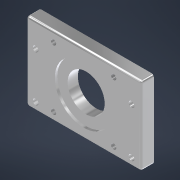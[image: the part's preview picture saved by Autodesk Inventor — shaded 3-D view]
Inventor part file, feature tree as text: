
AUTODESK INVENTOR PART (.ipt)
format: ipt  version: 2022 (Build 260153000, 153)  size: 172,032 bytes
history: native  units: mm
features: other x8, reference x6, sketch x3, extrude x2, hole x2, fillet x1, projected_geometry x1
ambient origin geometry x8: Origin, YZ Plane, XZ Plane, XY Plane, X Axis, Y Axis, Z Axis, Center Point
bodies: Solid1 (feature_tree)
feature tree (23):
  extrude  "Extrusion1"  Depth=8.0mm
  extrude  "Extrusion2"  Depth=2.0mm
  hole  "Hole2"  [1 undecoded]
  hole  "Hole3"  [1 undecoded]
  fillet  "Fillet1"  Radius=36.0mm
  sketch  "Sketch1"  dims[d2=8.0mm d3=0.0mm d6=31.0mm]
  reference  "Reference1"
  sketch  "Sketch6"  dims[d7=30.0mm]
  projected_geometry  "Projected Loop1"
  sketch  "Sketch7"  dims[d18=4.134mm d19=7.0mm d20=8.0mm d21=4.6mm d22=90.0deg d23=8.2mm d24=20.594885mm d25=45.0mm d26=2.0mm d27=0.0mm d28=75.0mm d29=36.0mm d30=6.0mm d31=4.5mm d32=6.0mm d33=8.0mm d34=4.6mm d35=90.0deg d36=8.0mm d37=20.594885mm d38=2.0mm d39=2.0mm d40=1.0mm d41=1.0mm d42=1.0mm d43=0.15mm d44=0.25mm d45=0.375mm d46=14.3117mm d47=0.75mm d48=20.594885mm d49=0.0625mm d50=0.75mm d51=0.375mm]
  reference  "Reference11"
  reference  "Reference12"
  reference  "Reference13"
  reference  "Reference14"
  reference  "Reference15"
  other  "SistemaElevacionV2.iam"
  other  "Soporte base:1"
  other  "ISO 4762 M4 x 12:3"
  other  "ISO 4762 M4 x 12:2"
  other  "ISO 4762 M4 x 12:4"
  other  "ISO 4762 M4 x 12:1"
  other  "Bevel Gears:1"
  other  "Bevel Gear2:1"
note: 2 required parameter values undecoded (feature->parameter linkage not recoverable at this tier; creation-order binding heuristic only, values carry confidence <= 0.55)
